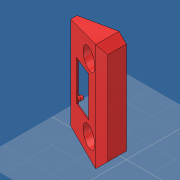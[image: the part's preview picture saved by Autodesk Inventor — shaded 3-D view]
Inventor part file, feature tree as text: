
AUTODESK INVENTOR PART (.ipt)
format: ipt  version: 2019 (Build 230136000, 136)  size: 264,704 bytes
history: native  units: mm
features: extrude x10, sketch x4, shell x1, hole x1, fillet x1, projected_geometry x1
ambient origin geometry x8: Origin, YZ Plane, XZ Plane, XY Plane, X Axis, Y Axis, Z Axis, Center Point
bodies: Volumenkörper1 (feature_tree)
feature tree (18):
  sketch  "Skizze2"  dims[d0=40.0mm d2=75.0mm d3=0.0mm d4=1.2mm]
  extrude  "Extrusion1"  Depth=1.2mm TaperAngle=0.0deg
  shell  "Wandung1"  Thickness=1.2mm
  sketch  "Skizze3"  dims[d12=35.75mm d13=3.0mm d16=75.0mm d17=0.0mm d20=2.0mm d21=0.0mm]
  extrude  "Extrusion2"  Depth=2.0mm TaperAngle=0.0deg
  extrude  "Extrusion4"  Depth=2.0mm TaperAngle=0.0deg
  extrude  "Extrusion11"  Depth=1.0mm
  extrude  "Extrusion15"  Depth=5.0mm
  sketch  "Skizze5"  dims[d30=16.0mm d34=2.0mm d35=0.0mm]
  extrude  "Extrusion7"  Depth=15.0mm
  extrude  "Extrusion8"  Depth=6.0mm
  extrude  "Extrusion10"  Depth=1.0mm
  hole  "Bohrung1"  [1 undecoded]
  sketch  "Skizze6"  dims[d36=2.0mm d37=0.0mm d38=1.0mm d40=5.0mm d43=15.0mm d45=6.0mm d46=21.816616mm d47=7.0mm d48=5.0mm d49=2.2mm d50=6.0mm d51=4.0mm d52=2.0mm d53=90.0deg d54=6.0mm d55=0.0mm d56=5.0mm d59=2.0mm d60=0.0mm d63=2.5mm d65=0.0mm d66=33.5mm d67=23.5mm d68=34.5mm d69=31.0mm d70=28.5mm d71=2.5mm d72=2.5mm d73=5.0mm d74=3.75mm d75=4.0mm d76=0.0mm d77=14.0mm d80=6.0mm d81=21.816616mm d82=0.0mm d83=1.0mm d84=0.0mm d87=1.0mm d88=0.0mm d90=0.5mm d91=0.5mm d92=0.0mm d93=5.0mm d94=1.0mm d95=1.0mm]
  extrude  "Extrusion12"  Depth=5.0mm
  extrude  "Extrusion14"  Depth=5.0mm
  fillet  "Rundung1"  Radius=2.0mm
  projected_geometry  "Projizierte Kontur1"
note: 1 required parameter value undecoded (feature->parameter linkage not recoverable at this tier; creation-order binding heuristic only, values carry confidence <= 0.55)
